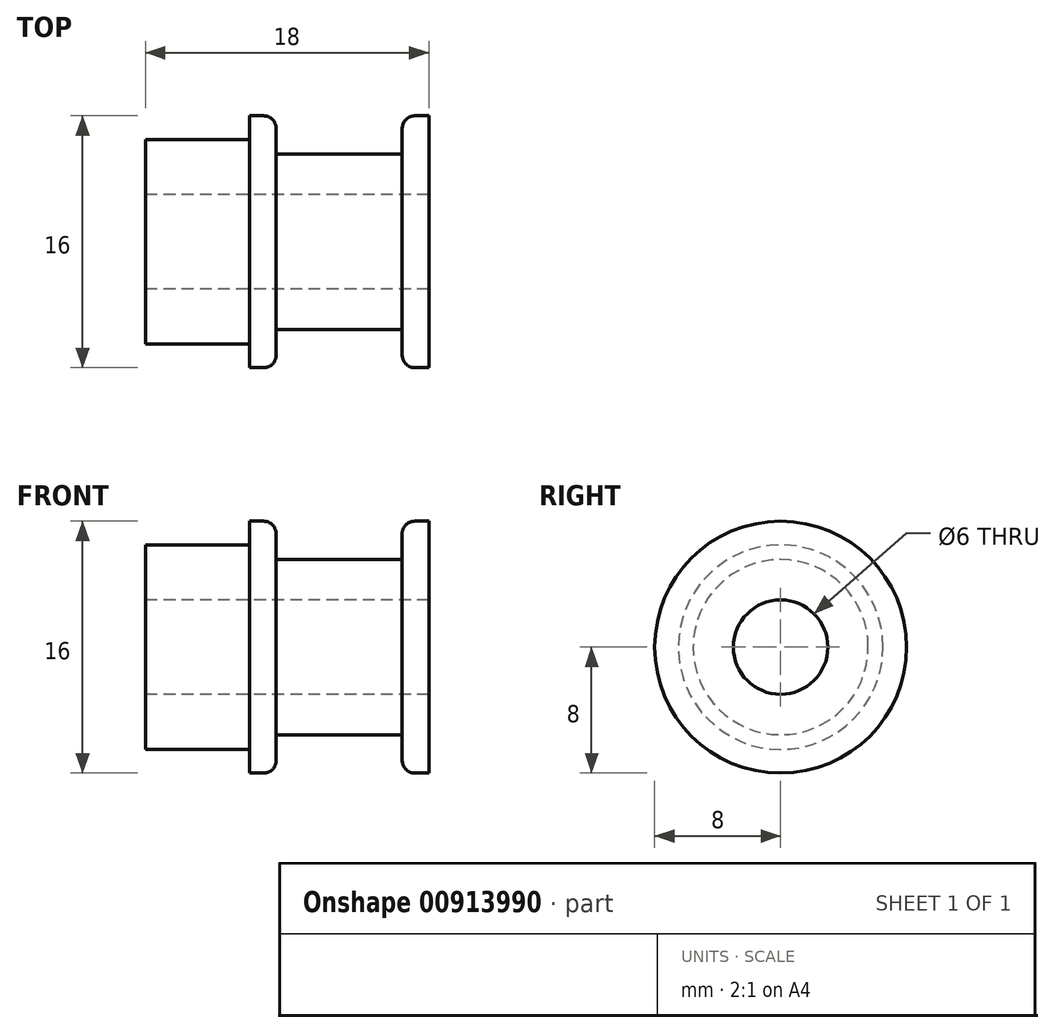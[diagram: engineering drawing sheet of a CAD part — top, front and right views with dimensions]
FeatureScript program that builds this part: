
annotation { "Feature Type Name" : "Feature", "Feature Type Description" : "" }
export const myFeature = defineFeature(function(context is Context, id is Id, definition is map)
    precondition{}
    {
        {
            var Q0;
            Q0=qCreatedBy(makeId("Front.planeOp"),FACE);
            var sketch = newSketch(context, id + "F0", { "sketchPlane" : qUnion([Q0])});
            skLineSegment(sketch, "E0", {"start": v(0, 0) * mm, "end": v(18, 0) * mm, "construction": true});
            skLineSegment(sketch, "E1", {"start": v(0, 3) * mm, "end": v(0, 6.5) * mm});
            skLineSegment(sketch, "E2", {"start": v(0, 6.5) * mm, "end": v(6.6, 6.5) * mm});
            skLineSegment(sketch, "E3", {"start": v(8.3, 5.56) * mm, "end": v(16.3, 5.56) * mm});
            skLineSegment(sketch, "E4", {"start": v(16.3, 5.56) * mm, "end": v(16.3, 8) * mm});
            skLineSegment(sketch, "E5", {"start": v(16.3, 8) * mm, "end": v(18, 8) * mm});
            skLineSegment(sketch, "E6", {"start": v(18, 8) * mm, "end": v(18, 3) * mm});
            skLineSegment(sketch, "E7", {"start": v(18, 3) * mm, "end": v(0, 3) * mm});
            skLineSegment(sketch, "E8", {"start": v(6.6, 6.5) * mm, "end": v(6.6, 8) * mm});
            skLineSegment(sketch, "E9", {"start": v(6.6, 8) * mm, "end": v(8.3, 8) * mm});
            skLineSegment(sketch, "E10", {"start": v(8.3, 8) * mm, "end": v(8.3, 5.56) * mm});
            skSolve(sketch);
        }
        {
            var Q0;
            Q0=makeQuery(id+"F0.imprint","IMPRINT",FACE,{"disambiguationData":[TD([[makeQuery(id+"F0.imprint","IMPRINT",EDGE,{"derivedFrom":sQuery(id+"F0.wireOp",EDGE,"E1")}),-1.0]])]});
            var Q1;
            Q1=sQuery(id+"F0.wireOp",EDGE,"E0");
            revolve(context, id + "F1", {"surfaceOperationType" : NewSurfaceOperationType.NEW, "entities" : qUnion([Q0]), "axis" : qUnion([Q1]), "revolveType" : RevolveType.FULL});
        }
        {
            var Q0;
            Q0=makeQuery(id+"F1.opRevolve","SWEPT_EDGE",EDGE,{"disambiguationData":[OSD([sQuery(id+"F0.wireOp",EDGE,"E9"),sQuery(id+"F0.wireOp",EDGE,"E10")])]});
            var Q1;
            Q1=makeQuery(id+"F1.opRevolve","SWEPT_EDGE",EDGE,{"disambiguationData":[OSD([sQuery(id+"F0.wireOp",EDGE,"E4"),sQuery(id+"F0.wireOp",EDGE,"E5")])]});
            fillet(context, id + "F2", {"entities" : qUnion([Q0, Q1]), "radius" : 0.8 * mm, "tangentPropagation" : true, "allowEdgeOverflow" : false});
        }
    });
